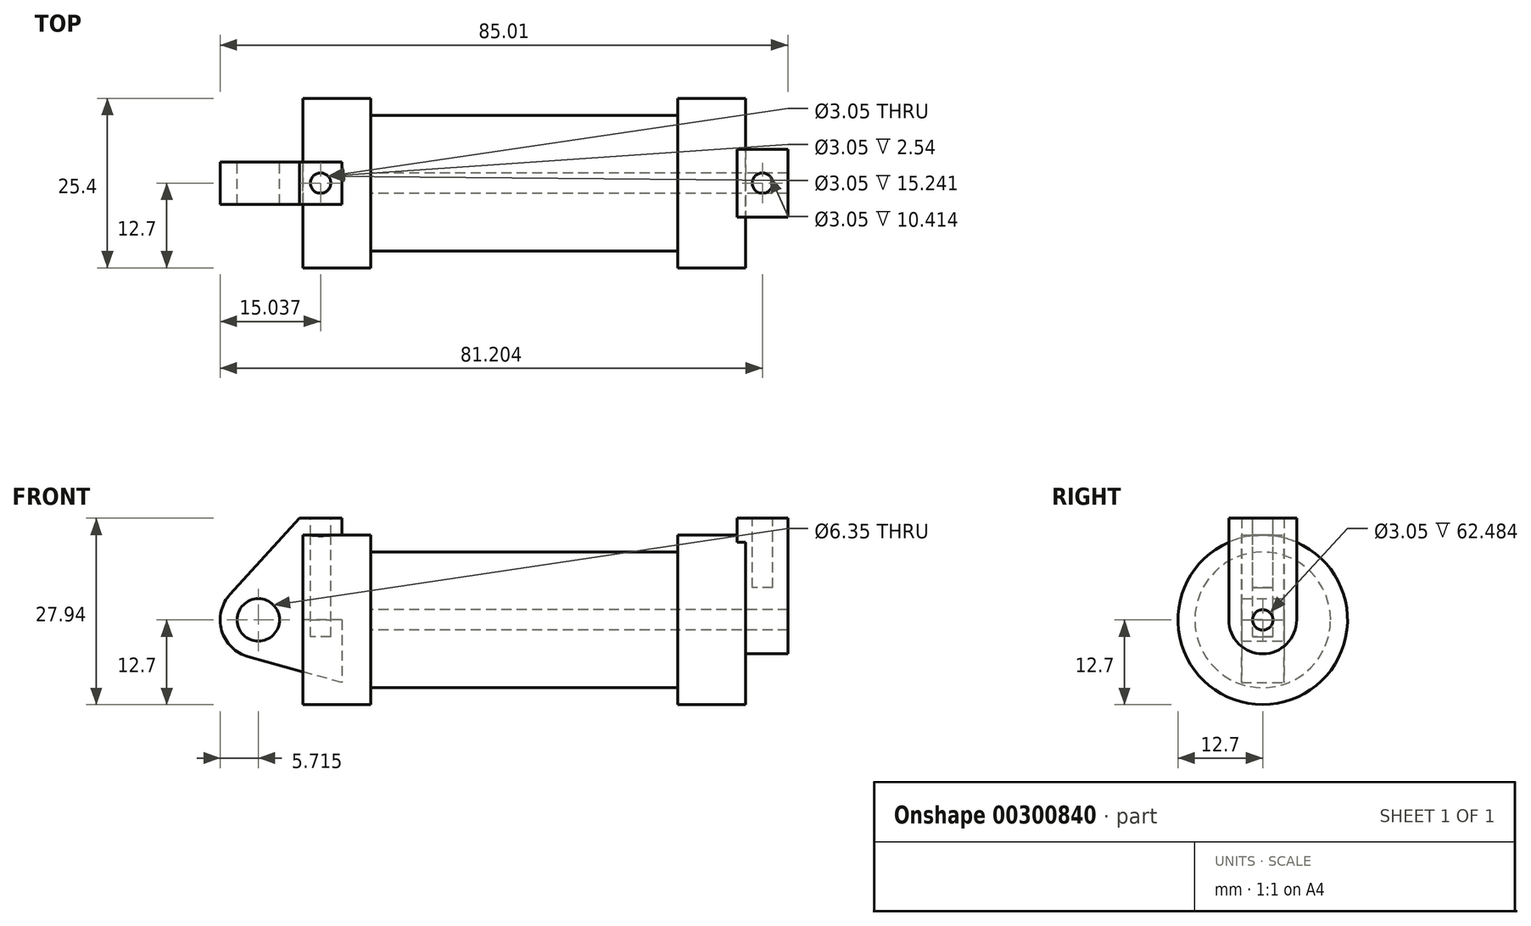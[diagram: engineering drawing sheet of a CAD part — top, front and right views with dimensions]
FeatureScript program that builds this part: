
annotation { "Feature Type Name" : "Feature", "Feature Type Description" : "" }
export const myFeature = defineFeature(function(context is Context, id is Id, definition is map)
    precondition{}
    {
        {
            var Q0;
            Q0=qCreatedBy(makeId("Front.planeOp"),FACE);
            var sketch = newSketch(context, id + "F0", { "sketchPlane" : qUnion([Q0])});
            skLineSegment(sketch, "E0", {"start": v(0, 0) * mm, "end": v(0, 12.7) * mm});
            skLineSegment(sketch, "E1", {"start": v(0, 12.7) * mm, "end": v(10.16, 12.7) * mm});
            skLineSegment(sketch, "E2", {"start": v(10.16, 12.7) * mm, "end": v(10.16, 10.16) * mm});
            skLineSegment(sketch, "E3", {"start": v(10.16, 10.16) * mm, "end": v(56.13, 10.16) * mm});
            skLineSegment(sketch, "E4", {"start": v(56.13, 10.16) * mm, "end": v(56.13, 12.7) * mm});
            skLineSegment(sketch, "E5", {"start": v(56.13, 12.7) * mm, "end": v(66.3, 12.7) * mm});
            skLineSegment(sketch, "E6", {"start": v(66.3, 12.7) * mm, "end": v(66.3, 0) * mm});
            skLineSegment(sketch, "E7", {"start": v(66.3, 0) * mm, "end": v(0, 0) * mm});
            skLineSegment(sketch, "E8", {"start": v(5.84, 15.24) * mm, "end": v(-0.5, 15.24) * mm});
            skLineSegment(sketch, "E9", {"start": v(-0.5, 15.24) * mm, "end": v(-10.88, 3.85) * mm});
            skLineSegment(sketch, "E10", {"start": v(0, 0) * mm, "end": v(-6.65, 0) * mm});
            skCircle(sketch, "E11", {"center": v(-6.65, 0) * mm, "radius": 5.72 * mm});
            skCircle(sketch, "E12", {"center": v(-6.65, 0) * mm, "radius": 3.18 * mm});
            skLineSegment(sketch, "E13", {"start": v(5.84, 15.24) * mm, "end": v(5.84, -9.4) * mm});
            skLineSegment(sketch, "E14", {"start": v(5.84, -9.4) * mm, "end": v(-8.18, -5.5) * mm});
            skSolve(sketch);
        }
        {
            var Q0;
            {var subQ0=sQuery(id+"F0.wireOp",EDGE,"E2");Q0=makeQuery(id+"F0.imprint","IMPRINT",FACE,{"disambiguationData":[TD([[makeQuery(id+"F0.imprint","IMPRINT",EDGE,{"derivedFrom":subQ0}),-1.0]])]});}
            var Q1;
            {var subQ0=sQuery(id+"F0.wireOp",EDGE,"E0");Q1=makeQuery(id+"F0.imprint","IMPRINT",FACE,{"disambiguationData":[TD([[makeQuery(id+"F0.imprint","IMPRINT",EDGE,{"derivedFrom":subQ0}),-1.0]])]});}
            var Q2;
            Q2=sQuery(id+"F0.wireOp",EDGE,"E7");
            revolve(context, id + "F1", {"entities" : qUnion([Q0, Q1]), "axis" : qUnion([Q2]), "revolveType" : RevolveType.FULL});
        }
        {
            var Q0;
            {var subQ0=sQuery(id+"F0.wireOp",EDGE,"E14");Q0=makeQuery(id+"F0.imprint","IMPRINT",FACE,{"disambiguationData":[TD([[makeQuery(id+"F0.imprint","IMPRINT",EDGE,{"derivedFrom":subQ0}),-1.0]])]});}
            var Q1;
            {var subQ1=sQuery(id+"F0.wireOp",EDGE,"E0");Q1=makeQuery(id+"F0.imprint","IMPRINT",FACE,{"disambiguationData":[TD([[makeQuery(id+"F0.imprint","IMPRINT",EDGE,{"derivedFrom":subQ1}),1.0]])]});}
            var Q2;
            {var subQ5=sQuery(id+"F0.wireOp",EDGE,"E12");Q2=makeQuery(id+"F0.imprint","IMPRINT",FACE,{"disambiguationData":[TD([[makeQuery(id+"F0.imprint","IMPRINT",EDGE,{"derivedFrom":subQ5}),-1.0]])]});}
            extrude(context, id + "F2", {"entities" : qUnion([Q0, Q1, Q2]), "endBound" : BoundingType.SYMMETRIC, "depth" : 6.35 * mm});
        }
        {
            var Q0;
            Q0=makeQuery(id+"F1.opRevolve","SWEPT_FACE",FACE,{"disambiguationData":[OSD([sQuery(id+"F0.wireOp",EDGE,"E6")])]});
            var sketch = newSketch(context, id + "F3", { "sketchPlane" : qUnion([Q0])});
            skCircle(sketch, "E15", {"center": v(0, 0) * mm, "radius": 1.52 * mm});
            skCircle(sketch, "E16", {"center": v(0, 0) * mm, "radius": 5.08 * mm});
            skLineSegment(sketch, "E17", {"start": v(5.08, 0) * mm, "end": v(5.08, 15.24) * mm});
            skLineSegment(sketch, "E18", {"start": v(-5.08, 0) * mm, "end": v(-5.08, 15.24) * mm});
            skLineSegment(sketch, "E19", {"start": v(-5.08, 15.24) * mm, "end": v(5.08, 15.24) * mm});
            skSolve(sketch);
        }
        {
            var Q0;
            {var subQ0=sQuery(id+"F3.wireOp",EDGE,"E19");Q0=makeQuery(id+"F3.imprint","IMPRINT",FACE,{"disambiguationData":[TD([[makeQuery(id+"F3.imprint","IMPRINT",EDGE,{"derivedFrom":subQ0}),-1.0]])]});}
            var Q1;
            {var subQ0=sQuery(id+"F3.wireOp",EDGE,"E17");var subQ1=sQuery(id+"F3.wireOp",EDGE,"E16");var subQ2=makeQuery(id+"F3.imprint","INTERSECT",VERTEX,{"derivedFrom":[subQ1,subQ0]});Q1=makeQuery(id+"F3.imprint","IMPRINT",FACE,{"disambiguationData":[TD([[makeQuery(id+"F3.imprint","IMPRINT",EDGE,{"disambiguationData":[TD([[subQ2,-1.0]])],"derivedFrom":subQ1}),-1.0]])]});}
            var Q2;
            Q2=makeQuery(id+"F3.imprint","IMPRINT",FACE,{"disambiguationData":[TD([[makeQuery(id+"F3.imprint","IMPRINT",EDGE,{"derivedFrom":sQuery(id+"F3.wireOp",EDGE,"E15")}),-1.0]])]});
            extrude(context, id + "F4", {"entities" : qUnion([Q0, Q1, Q2]), "operationType" : NewBodyOperationType.ADD, "depth" : 6.35 * mm, "hasSecondDirection" : true, "secondDirectionOppositeDirection" : true, "secondDirectionDepth" : 1.27 * mm});
        }
        {
            var Q0;
            Q0=makeQuery(id+"F4.boolean.opBoolean","SPLIT",FACE,{"disambiguationData":[TD([makeQuery(id+"F4.opExtrude","SWEPT_FACE",FACE,{"disambiguationData":[OSD([sQuery(id+"F3.wireOp",EDGE,"E15")])]})])],"derivedFrom":makeQuery(id+"F1.opRevolve","SWEPT_FACE",FACE,{"disambiguationData":[OSD([sQuery(id+"F0.wireOp",EDGE,"E6")])]})});
            var Q1;
            Q1=makeQuery(id+"F1.opRevolve","SWEPT_FACE",FACE,{"disambiguationData":[OSD([sQuery(id+"F0.wireOp",EDGE,"E2")])]});
            extrude(context, id + "F5", {"entities" : qUnion([Q0]), "operationType" : NewBodyOperationType.REMOVE, "endBound" : BoundingType.UP_TO_SURFACE, "oppositeDirection" : true, "endBoundEntityFace" : qUnion([Q1]), "depth" : 25.4 * mm});
        }
        {
            var Q0;
            Q0=makeQuery(id+"F2.opExtrude","SWEPT_FACE",FACE,{"disambiguationData":[OSD([sQuery(id+"F0.wireOp",EDGE,"E8")])]});
            var sketch = newSketch(context, id + "F6", { "sketchPlane" : qUnion([Q0])});
            skLineSegment(sketch, "E20.0.0", {"start": v(5.84, 3.18) * mm, "end": v(-0.5, 3.18) * mm});
            skLineSegment(sketch, "E20.0.1", {"start": v(-0.5, 3.17) * mm, "end": v(-0.5, -3.18) * mm});
            skLineSegment(sketch, "E20.0.2", {"start": v(-0.5, -3.18) * mm, "end": v(5.84, -3.18) * mm});
            skLineSegment(sketch, "E20.0.3", {"start": v(5.84, -3.18) * mm, "end": v(5.84, 3.17) * mm});
            skCircle(sketch, "E21", {"center": v(2.67, 0) * mm, "radius": 1.52 * mm});
            skPoint(sketch, "E21.centerSnap0", {"position": v(5.84, 0) * mm});
            skPoint(sketch, "E21.centerSnap1", {"position": v(2.67, -3.18) * mm});
            skSolve(sketch);
        }
        {
            var Q0;
            Q0=makeQuery(id+"F4.opExtrude","SWEPT_FACE",FACE,{"disambiguationData":[OSD([sQuery(id+"F3.wireOp",EDGE,"E19")])]});
            var sketch = newSketch(context, id + "F7", { "sketchPlane" : qUnion([Q0])});
            skCircle(sketch, "E22", {"center": v(68.83, 0) * mm, "radius": 1.52 * mm});
            skPoint(sketch, "E22.centerSnap0", {"position": v(72.64, 0) * mm});
            skPoint(sketch, "E22.centerSnap1", {"position": v(68.83, 5.08) * mm});
            skSolve(sketch);
        }
        {
            var Q0;
            Q0=makeQuery(id+"F6.imprint","IMPRINT",FACE,{"disambiguationData":[TD([[makeQuery(id+"F6.imprint","IMPRINT",EDGE,{"derivedFrom":sQuery(id+"F6.wireOp",EDGE,"E21")}),1.0]])]});
            extrude(context, id + "F8", {"entities" : qUnion([Q0]), "operationType" : NewBodyOperationType.REMOVE, "oppositeDirection" : true, "depth" : 17.78 * mm});
        }
        {
            var Q0;
            Q0=makeQuery(id+"F7.imprint","IMPRINT",FACE,{"disambiguationData":[TD([[makeQuery(id+"F7.imprint","IMPRINT",EDGE,{"derivedFrom":sQuery(id+"F7.wireOp",EDGE,"E22")}),1.0]])]});
            extrude(context, id + "F9", {"entities" : qUnion([Q0]), "operationType" : NewBodyOperationType.REMOVE, "oppositeDirection" : true, "depth" : 10.4 * mm});
        }
    });
